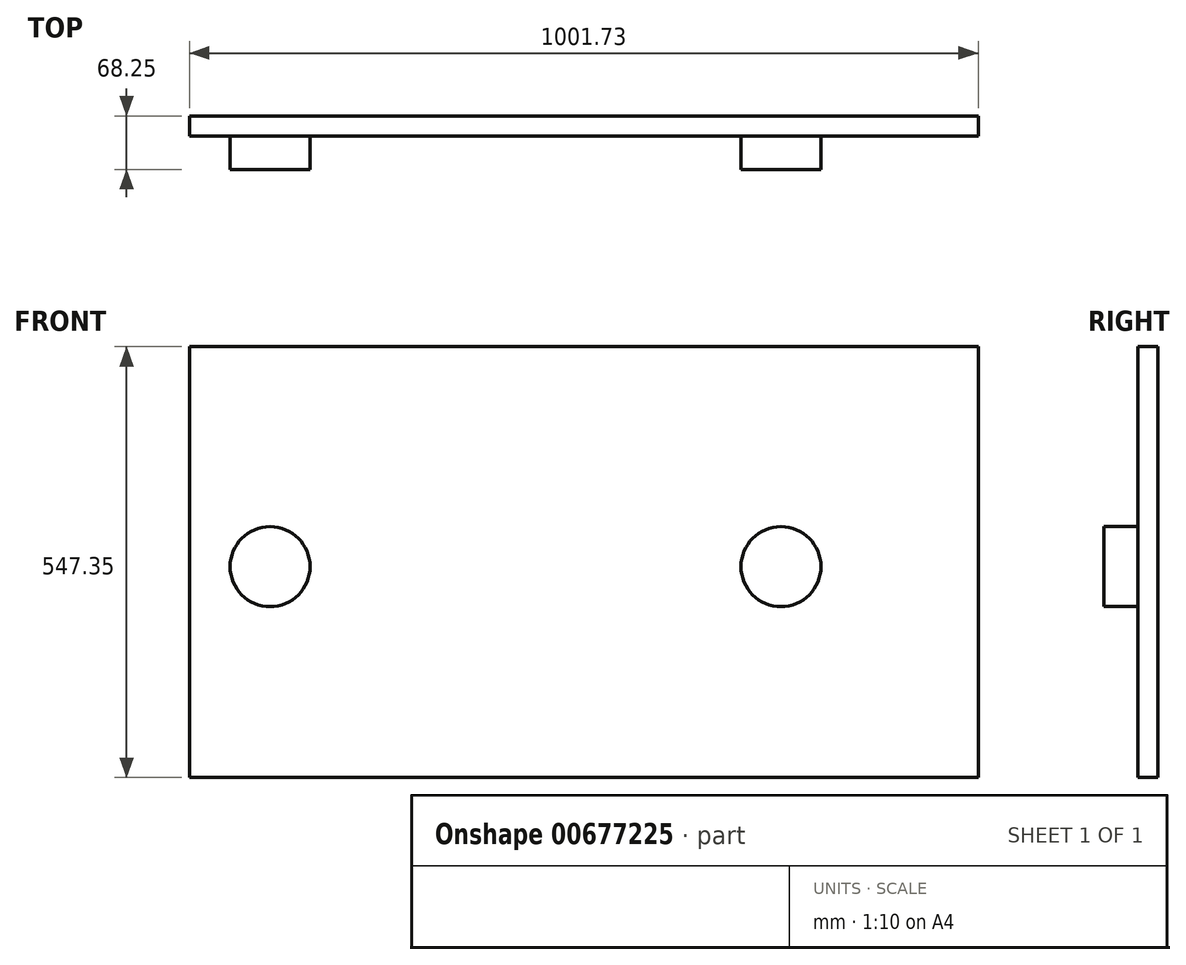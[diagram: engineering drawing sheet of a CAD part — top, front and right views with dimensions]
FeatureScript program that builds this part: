
annotation { "Feature Type Name" : "Feature", "Feature Type Description" : "" }
export const myFeature = defineFeature(function(context is Context, id is Id, definition is map)
    precondition{}
    {
        {
            var Q0;
            Q0=qCreatedBy(makeId("Front.planeOp"),FACE);
            var sketch = newSketch(context, id + "F0", { "sketchPlane" : qUnion([Q0])});
            skLineSegment(sketch, "E0.bottom", {"start": v(-520.94, 233.08) * mm, "end": v(480.8, 233.08) * mm});
            skLineSegment(sketch, "E0.top", {"start": v(-520.94, -314.27) * mm, "end": v(480.8, -314.27) * mm});
            skLineSegment(sketch, "E0.left", {"start": v(-520.94, 233.08) * mm, "end": v(-520.94, -314.27) * mm});
            skLineSegment(sketch, "E0.right", {"start": v(480.8, 233.08) * mm, "end": v(480.8, -314.27) * mm});
            skSolve(sketch);
        }
        {
            var Q0;
            Q0 = qSketchRegion(id + "F0", true);
            extrude(context, id + "F1", {"entities" : qUnion([Q0]), "depth" : 25.4 * mm, "offsetDistance" : 25.4 * mm});
        }
        {
            var Q0;
            Q0=qCreatedBy(makeId("Front.planeOp"),FACE);
            var sketch = newSketch(context, id + "F2", { "sketchPlane" : qUnion([Q0])});
            skCircle(sketch, "E1", {"center": v(-418.65, -46.26) * mm, "radius": 50.8 * mm});
            skLineSegment(sketch, "E2", {"start": v(-418.65, -46.26) * mm, "end": v(230.32, -46.26) * mm});
            skCircle(sketch, "E3", {"center": v(230.32, -46.26) * mm, "radius": 50.8 * mm});
            skSolve(sketch);
        }
        {
            var Q0;
            Q0 = qSketchRegion(id + "F2", true);
            extrude(context, id + "F3", {"entities" : qUnion([Q0]), "operationType" : NewBodyOperationType.ADD, "depth" : 68.25 * mm, "offsetDistance" : 25.4 * mm});
        }
    });
